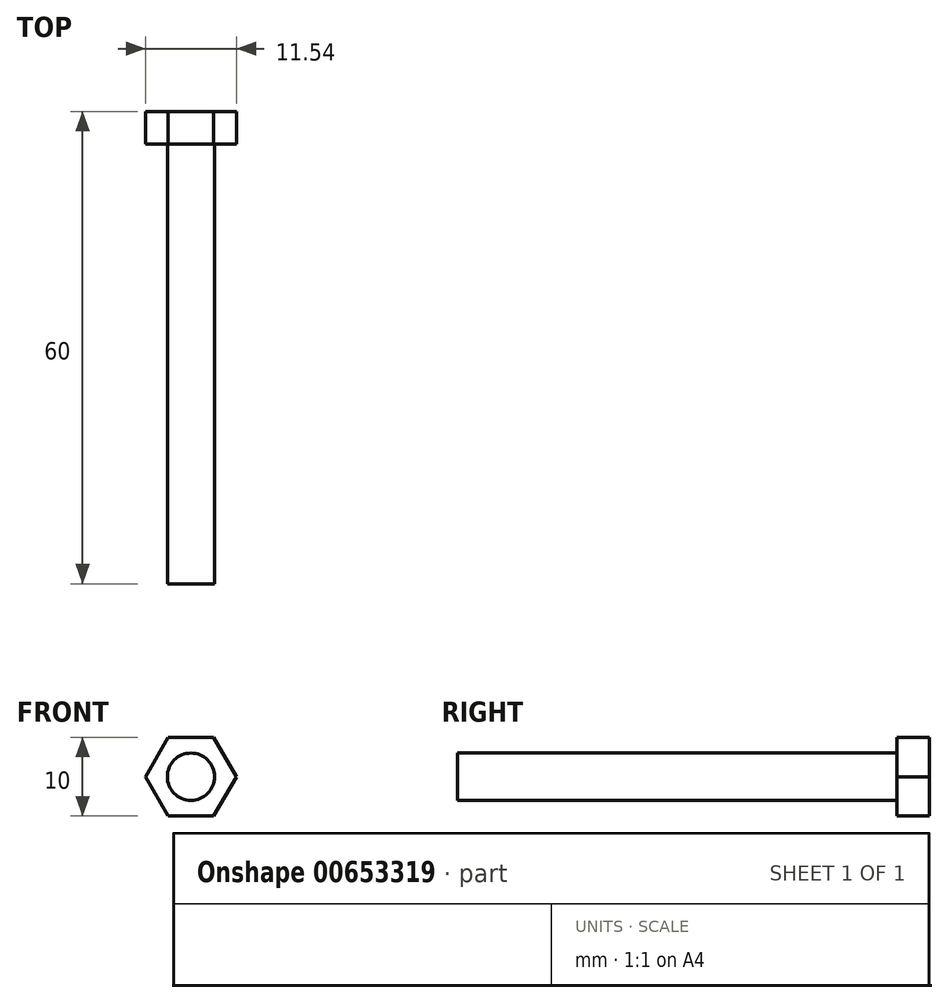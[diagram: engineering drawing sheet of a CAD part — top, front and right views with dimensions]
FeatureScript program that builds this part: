
annotation { "Feature Type Name" : "Feature", "Feature Type Description" : "" }
export const myFeature = defineFeature(function(context is Context, id is Id, definition is map)
    precondition{}
    {
        {
            var Q0;
            Q0=qCreatedBy(makeId("Front.planeOp"),FACE);
            var sketch = newSketch(context, id + "F0", { "sketchPlane" : qUnion([Q0])});
            skCircle(sketch, "E0.cCircle", {"center": v(0, 0) * mm, "radius": 5 * mm, "construction": true});
            skLineSegment(sketch, "E0.0", {"start": v(-2.89, 5) * mm, "end": v(2.89, 5) * mm});
            skLineSegment(sketch, "E0.1", {"start": v(2.89, 5) * mm, "end": v(5.77, 0) * mm});
            skLineSegment(sketch, "E0.2", {"start": v(5.77, 0) * mm, "end": v(2.89, -5) * mm});
            skLineSegment(sketch, "E0.3", {"start": v(2.89, -5) * mm, "end": v(-2.89, -5) * mm});
            skLineSegment(sketch, "E0.4", {"start": v(-2.89, -5) * mm, "end": v(-5.77, 0) * mm});
            skLineSegment(sketch, "E0.5", {"start": v(-5.77, 0) * mm, "end": v(-2.89, 5) * mm});
            skPoint(sketch, "E0.0.midPoint", {"position": v(0, 5) * mm});
            skCircle(sketch, "E1", {"center": v(0, 0) * mm, "radius": 3 * mm});
            skSolve(sketch);
        }
        {
            var Q0;
            Q0=makeQuery(id+"F0.imprint","IMPRINT",FACE,{"disambiguationData":[TD([[makeQuery(id+"F0.imprint","IMPRINT",EDGE,{"derivedFrom":sQuery(id+"F0.wireOp",EDGE,"E0.0")}),-1.0]])]});
            var Q1;
            Q1=makeQuery(id+"F0.imprint","IMPRINT",FACE,{"disambiguationData":[TD([[makeQuery(id+"F0.imprint","IMPRINT",EDGE,{"derivedFrom":sQuery(id+"F0.wireOp",EDGE,"E1")}),1.0]])]});
            extrude(context, id + "F1", {"entities" : qUnion([Q0, Q1]), "depth" : 4.15 * mm, "offsetDistance" : 25 * mm});
        }
        {
            var Q0;
            Q0=makeQuery(id+"F0.imprint","IMPRINT",FACE,{"disambiguationData":[TD([[makeQuery(id+"F0.imprint","IMPRINT",EDGE,{"derivedFrom":sQuery(id+"F0.wireOp",EDGE,"E1")}),1.0]])]});
            extrude(context, id + "F2", {"entities" : qUnion([Q0]), "operationType" : NewBodyOperationType.ADD, "depth" : 60 * mm, "offsetDistance" : 25 * mm});
        }
    });
